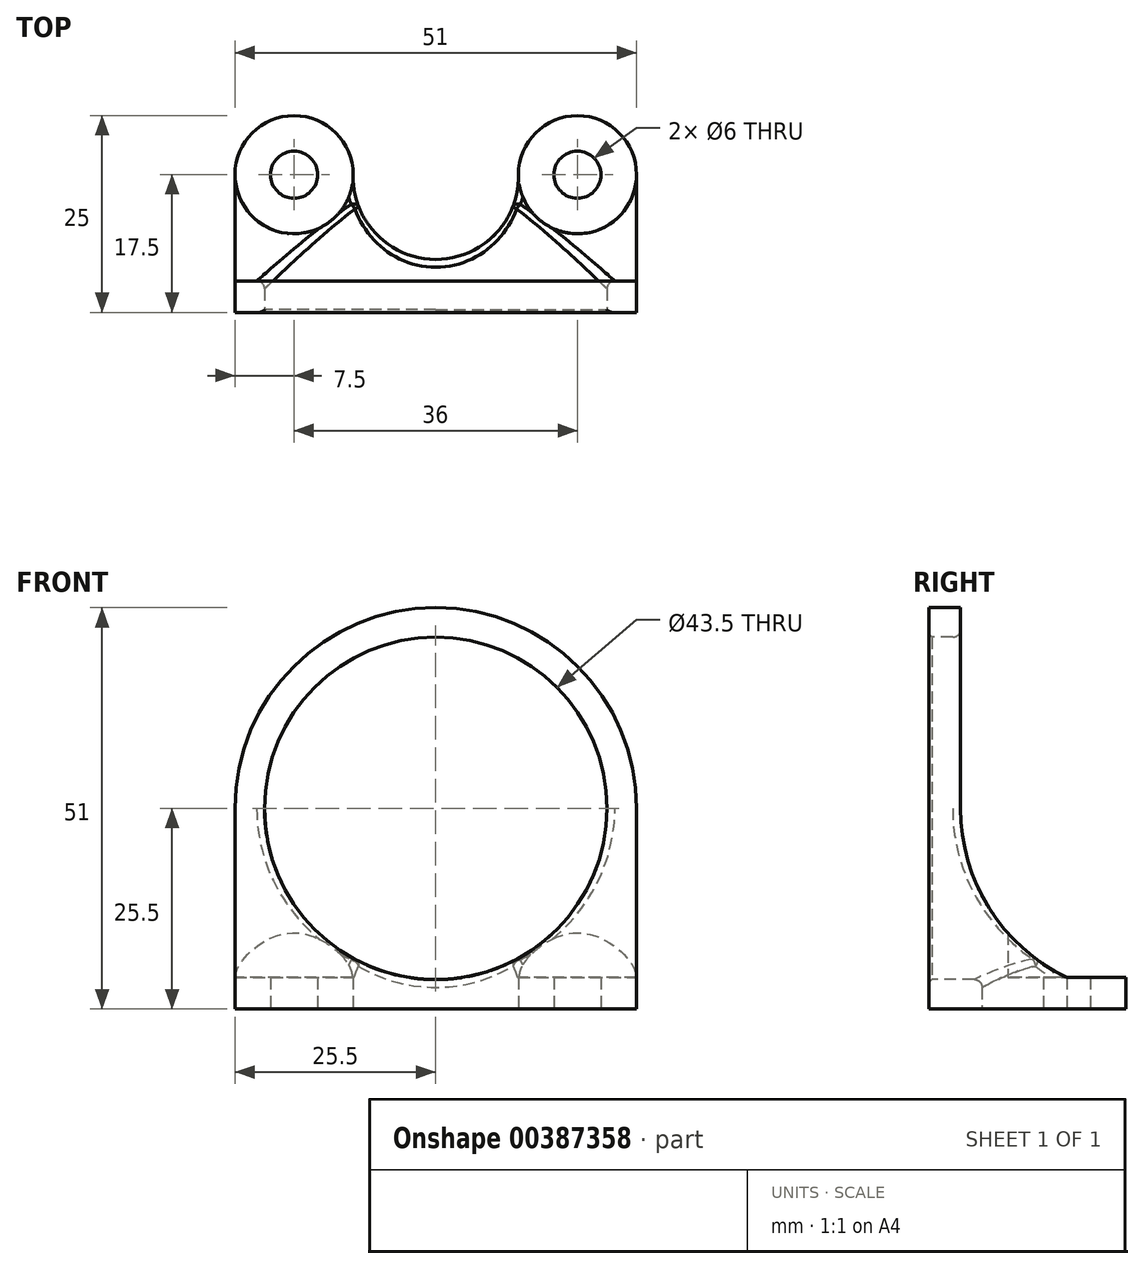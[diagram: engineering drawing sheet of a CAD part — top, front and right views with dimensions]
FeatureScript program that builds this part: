
annotation { "Feature Type Name" : "Feature", "Feature Type Description" : "" }
export const myFeature = defineFeature(function(context is Context, id is Id, definition is map)
    precondition{}
    {
        {
            var Q0;
            Q0=qCreatedBy(makeId("Front.planeOp"),FACE);
            var sketch = newSketch(context, id + "F0", { "sketchPlane" : qUnion([Q0])});
            skCircle(sketch, "E0", {"center": v(0, 0) * mm, "radius": 21.5 * mm});
            skPoint(sketch, "E1", {"position": v(25.5, 0) * mm});
            skPoint(sketch, "E2", {"position": v(-25.5, 0) * mm});
            skLineSegment(sketch, "E3", {"start": v(0, 0) * mm, "end": v(0, -25.5) * mm});
            skArc(sketch, "E4", {"start": v(25.5, 0) * mm, "mid": v(0, 25.5) * mm, "end": v(-25.5, 0) * mm});
            skCircle(sketch, "E5", {"center": v(0, 0) * mm, "radius": 25.5 * mm, "construction": true});
            skArc(sketch, "E6", {"start": v(-21.5, -13.71) * mm, "mid": v(-18.03, -18.03) * mm, "end": v(-13.71, -21.5) * mm});
            skArc(sketch, "E7", {"start": v(21.5, -13.71) * mm, "mid": v(18.03, -18.03) * mm, "end": v(13.71, -21.5) * mm});
            skPoint(sketch, "E8.visualSharp", {"position": v(-25.5, -21.5) * mm});
            skPoint(sketch, "E9.visualSharp", {"position": v(25.5, -21.5) * mm});
            skPoint(sketch, "E10.visualSharp", {"position": v(21.5, -21.5) * mm});
            skPoint(sketch, "E11.visualSharp", {"position": v(-21.5, -21.5) * mm});
            skLineSegment(sketch, "E12", {"start": v(25.5, 0) * mm, "end": v(25.5, -25.5) * mm});
            skLineSegment(sketch, "E13", {"start": v(-25.5, 0) * mm, "end": v(-25.5, -25.5) * mm});
            skLineSegment(sketch, "E14", {"start": v(25.5, -25.5) * mm, "end": v(-25.5, -25.5) * mm});
            skSolve(sketch);
        }
        {
            var Q0;
            Q0=makeQuery(id+"F0.imprint","IMPRINT",FACE,{"disambiguationData":[TD([[makeQuery(id+"F0.imprint","IMPRINT",EDGE,{"derivedFrom":sQuery(id+"F0.wireOp",EDGE,"E0")}),-1.0]])]});
            extrude(context, id + "F1", {"entities" : qUnion([Q0]), "oppositeDirection" : true, "depth" : 4 * mm});
        }
        {
            var Q0;
            Q0=makeQuery(id+"F0.imprint","IMPRINT",FACE,{"disambiguationData":[TD([[makeQuery(id+"F0.imprint","IMPRINT",EDGE,{"derivedFrom":sQuery(id+"F0.wireOp",EDGE,"E0")}),1.0]])]});
            extrude(context, id + "F2", {"entities" : qUnion([Q0]), "operationType" : NewBodyOperationType.REMOVE, "endBound" : BoundingType.THROUGH_ALL, "oppositeDirection" : true, "depth" : 40 * mm});
        }
        {
            var Q0;
            Q0=makeQuery(id+"F1.opExtrude","SWEPT_FACE",FACE,{"disambiguationData":[OSD([sQuery(id+"F0.wireOp",EDGE,"E14")])]});
            var sketch = newSketch(context, id + "F3", { "sketchPlane" : qUnion([Q0])});
            skLineSegment(sketch, "E15", {"start": v(25.5, 0) * mm, "end": v(25.5, -17.5) * mm});
            skLineSegment(sketch, "E16", {"start": v(-25.5, 0) * mm, "end": v(-25.5, -17.5) * mm});
            skLineSegment(sketch, "E17", {"start": v(25.5, 0) * mm, "end": v(-25.5, 0) * mm});
            skLineSegment(sketch, "E18", {"start": v(25.5, 0) * mm, "end": v(25.5, -10) * mm, "construction": true});
            skLineSegment(sketch, "E19", {"start": v(25.5, -10) * mm, "end": v(-25.5, -10) * mm, "construction": true});
            skLineSegment(sketch, "E20", {"start": v(25.5, -17.5) * mm, "end": v(10.5, -17.5) * mm, "construction": true});
            skLineSegment(sketch, "E21", {"start": v(-25.5, -17.5) * mm, "end": v(-10.5, -17.5) * mm, "construction": true});
            skPoint(sketch, "E22", {"position": v(18, -17.5) * mm});
            skPoint(sketch, "E23", {"position": v(-18, -17.5) * mm});
            skArc(sketch, "E24", {"start": v(25.5, -17.5) * mm, "mid": v(18, -25) * mm, "end": v(10.5, -17.5) * mm});
            skArc(sketch, "E25", {"start": v(-10.5, -17.5) * mm, "mid": v(-18.21, -25) * mm, "end": v(-25.49, -17.08) * mm});
            skCircle(sketch, "E26", {"center": v(18, -17.5) * mm, "radius": 3 * mm});
            skCircle(sketch, "E27", {"center": v(-18, -17.5) * mm, "radius": 3 * mm});
            skPoint(sketch, "E28", {"position": v(0, -4) * mm});
            skArc(sketch, "E29", {"start": v(10.5, -17.5) * mm, "mid": v(0, -6.74) * mm, "end": v(-10.5, -17.5) * mm});
            skSolve(sketch);
        }
        {
            var Q0;
            {var subQ4=sQuery(id+"F3.wireOp",EDGE,"E15");Q0=makeQuery(id+"F3.imprint","IMPRINT",FACE,{"disambiguationData":[TD([[makeQuery(id+"F3.imprint","IMPRINT",EDGE,{"derivedFrom":subQ4}),-1.0]])]});}
            var Q1;
            {var subQ4=sQuery(id+"F3.wireOp",EDGE,"E16");Q1=makeQuery(id+"F3.imprint","IMPRINT",FACE,{"disambiguationData":[TD([[makeQuery(id+"F3.imprint","IMPRINT",EDGE,{"derivedFrom":subQ4}),1.0]])]});}
            extrude(context, id + "F4", {"entities" : qUnion([Q0, Q1]), "operationType" : NewBodyOperationType.ADD, "oppositeDirection" : true, "depth" : 25.5 * mm});
        }
        {
            var Q0;
            {var subQ0=sQuery(id+"F0.wireOp",EDGE,"E14");Q0=makeQuery(id+"F4.boolean.opBoolean","MERGE",FACE,{"derivedFrom":[makeQuery(id+"F1.opExtrude","SWEPT_FACE",FACE,{"disambiguationData":[OSD([subQ0])]}),makeQuery(id+"F4.opExtrude","CAP_FACE",FACE,{"disambiguationData":[OSD([subQ0,sQuery(id+"F3.wireOp",EDGE,"E15"),sQuery(id+"F3.wireOp",EDGE,"E16"),sQuery(id+"F3.wireOp",EDGE,"E24"),sQuery(id+"F3.wireOp",EDGE,"E25"),sQuery(id+"F3.wireOp",EDGE,"E26"),sQuery(id+"F3.wireOp",EDGE,"E27"),sQuery(id+"F3.wireOp",EDGE,"E29")])],"isStart":true})]});}
            var sketch = newSketch(context, id + "F5", { "sketchPlane" : qUnion([Q0])});
            skPoint(sketch, "E30", {"position": v(18, -17.5) * mm});
            skPoint(sketch, "E31", {"position": v(-18, -17.5) * mm});
            skCircle(sketch, "E32", {"center": v(18, -17.5) * mm, "radius": 7.5 * mm});
            skCircle(sketch, "E33", {"center": v(-18, -17.5) * mm, "radius": 7.5 * mm});
            skSolve(sketch);
        }
        {
            var Q0;
            Q0=makeQuery(id+"F5.imprint","IMPRINT",FACE,{"disambiguationData":[TD([[makeQuery(id+"F5.imprint","IMPRINT",EDGE,{"derivedFrom":makeQuery(id+"F4.opExtrude","CAP_EDGE",EDGE,{"disambiguationData":[OSD([sQuery(id+"F3.wireOp",EDGE,"E26")])],"isStart":true})}),-1.0]])]});
            var Q1;
            Q1=makeQuery(id+"F5.imprint","IMPRINT",FACE,{"disambiguationData":[TD([[makeQuery(id+"F5.imprint","IMPRINT",EDGE,{"derivedFrom":makeQuery(id+"F4.opExtrude","CAP_EDGE",EDGE,{"disambiguationData":[OSD([sQuery(id+"F3.wireOp",EDGE,"E27")])],"isStart":true})}),-1.0]])]});
            extrude(context, id + "F6", {"entities" : qUnion([Q0, Q1]), "operationType" : NewBodyOperationType.REMOVE, "endBound" : BoundingType.THROUGH_ALL, "oppositeDirection" : true, "depth" : 30 * mm, "hasSecondDirection" : true, "secondDirectionOppositeDirection" : true, "secondDirectionDepth" : 4 * mm, "offsetDistance" : 25 * mm});
        }
        {
            var Q0;
            Q0=makeQuery(id+"F4.boolean.opBoolean","MERGE",FACE,{"derivedFrom":[makeQuery(id+"F1.opExtrude","SWEPT_FACE",FACE,{"disambiguationData":[OSD([sQuery(id+"F0.wireOp",EDGE,"E13")])]}),makeQuery(id+"F4.opExtrude","SWEPT_FACE",FACE,{"disambiguationData":[OSD([sQuery(id+"F3.wireOp",EDGE,"E16")])]})]});
            var sketch = newSketch(context, id + "F7", { "sketchPlane" : qUnion([Q0])});
            skLineSegment(sketch, "E34", {"start": v(-17.5, -21.5) * mm, "end": v(-4, -21.5) * mm});
            skLineSegment(sketch, "E35", {"start": v(-4, -21.5) * mm, "end": v(-4, 0) * mm});
            skArc(sketch, "E36", {"start": v(-17.5, -21.5) * mm, "mid": v(-7.65, -12.7) * mm, "end": v(-4, 0) * mm});
            skLineSegment(sketch, "E37", {"start": v(-17.5, -21.5) * mm, "end": v(-17.5, 0) * mm});
            skLineSegment(sketch, "E38", {"start": v(-17.5, 0) * mm, "end": v(-4, 0) * mm});
            skSolve(sketch);
        }
        {
            var Q0;
            Q0=makeQuery(id+"F7.imprint","IMPRINT",FACE,{"disambiguationData":[TD([[makeQuery(id+"F7.imprint","IMPRINT",EDGE,{"derivedFrom":sQuery(id+"F7.wireOp",EDGE,"E36")}),1.0]])]});
            extrude(context, id + "F8", {"entities" : qUnion([Q0]), "operationType" : NewBodyOperationType.REMOVE, "endBound" : BoundingType.THROUGH_ALL, "oppositeDirection" : true, "depth" : 25 * mm});
        }
        {
            var Q0;
            Q0=makeQuery(id+"F1.opExtrude","CAP_EDGE",EDGE,{"disambiguationData":[OSD([sQuery(id+"F0.wireOp",EDGE,"E0")])],"isStart":true});
            fillet(context, id + "F9", {"entities" : qUnion([Q0]), "radius" : 1 * mm, "tangentPropagation" : true, "allowEdgeOverflow" : false});
        }
        {
            var Q0;
            Q0=makeQuery(id+"F1.opExtrude","CAP_FACE",FACE,{"disambiguationData":[OSD([sQuery(id+"F0.wireOp",EDGE,"E0"),sQuery(id+"F0.wireOp",EDGE,"E4"),sQuery(id+"F0.wireOp",EDGE,"E12"),sQuery(id+"F0.wireOp",EDGE,"E13"),sQuery(id+"F0.wireOp",EDGE,"E14")])],"isStart":true});
            var sketch = newSketch(context, id + "F10", { "sketchPlane" : qUnion([Q0])});
            skPoint(sketch, "E39", {"position": v(0, 0) * mm});
            skCircle(sketch, "E40", {"center": v(0, 0) * mm, "radius": 21.75 * mm});
            skSolve(sketch);
        }
        {
            var Q0;
            Q0=makeQuery(id+"F10.imprint","IMPRINT",FACE,{"disambiguationData":[TD([[makeQuery(id+"F10.imprint","IMPRINT",EDGE,{"derivedFrom":sQuery(id+"F10.wireOp",EDGE,"E40")}),1.0]])]});
            extrude(context, id + "F11", {"entities" : qUnion([Q0]), "operationType" : NewBodyOperationType.REMOVE, "endBound" : BoundingType.THROUGH_ALL, "oppositeDirection" : true, "depth" : 25 * mm});
        }
        {
            var Q0;
            {var subQ0=sQuery(id+"F0.wireOp",EDGE,"E0");Q0=makeQuery(id+"F4.boolean.opBoolean","SPLIT",EDGE,{"disambiguationData":[topologyDisambiguationEdgeConnected([makeQuery(id+"F1.opExtrude","CAP_FACE",FACE,{"disambiguationData":[OSD([subQ0,sQuery(id+"F0.wireOp",EDGE,"E4"),sQuery(id+"F0.wireOp",EDGE,"E12"),sQuery(id+"F0.wireOp",EDGE,"E13"),sQuery(id+"F0.wireOp",EDGE,"E14")])],"isStart":false})])],"derivedFrom":makeQuery(id+"F1.opExtrude","CAP_EDGE",EDGE,{"disambiguationData":[OSD([subQ0])],"isStart":false})});}
            var Q1;
            Q1=makeQuery(id+"F11.boolean.opBoolean","INTERSECT",EDGE,{"disambiguationData":[OD(0.0)],"derivedFrom":[makeQuery(id+"F8.boolean.opBoolean","COPY",FACE,{"derivedFrom":makeQuery(id+"F8.opExtrude","SWEPT_FACE",FACE,{"disambiguationData":[OSD([sQuery(id+"F7.wireOp",EDGE,"E36")])]})}),makeQuery(id+"F11.opExtrude","SWEPT_FACE",FACE,{"disambiguationData":[OSD([sQuery(id+"F10.wireOp",EDGE,"E40")])]})]});
            var Q2;
            Q2=makeQuery(id+"F11.boolean.opBoolean","INTERSECT",EDGE,{"disambiguationData":[OD(1.0)],"derivedFrom":[makeQuery(id+"F8.boolean.opBoolean","COPY",FACE,{"derivedFrom":makeQuery(id+"F8.opExtrude","SWEPT_FACE",FACE,{"disambiguationData":[OSD([sQuery(id+"F7.wireOp",EDGE,"E36")])]})}),makeQuery(id+"F11.opExtrude","SWEPT_FACE",FACE,{"disambiguationData":[OSD([sQuery(id+"F10.wireOp",EDGE,"E40")])]})]});
            fillet(context, id + "F12", {"entities" : qUnion([Q0, Q1, Q2]), "radius" : 1 * mm, "tangentPropagation" : true, "allowEdgeOverflow" : false});
        }
        {
            var Q0;
            Q0=makeQuery(id+"F11.boolean.opBoolean","INTERSECT",EDGE,{"derivedFrom":[makeQuery(id+"F4.opExtrude","SWEPT_FACE",FACE,{"disambiguationData":[OSD([sQuery(id+"F3.wireOp",EDGE,"E29")])]}),makeQuery(id+"F11.opExtrude","SWEPT_FACE",FACE,{"disambiguationData":[OSD([sQuery(id+"F10.wireOp",EDGE,"E40")])]})]});
            fillet(context, id + "F13", {"entities" : qUnion([Q0]), "radius" : 1 * mm, "tangentPropagation" : true, "allowEdgeOverflow" : false});
        }
    });
